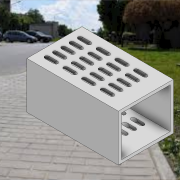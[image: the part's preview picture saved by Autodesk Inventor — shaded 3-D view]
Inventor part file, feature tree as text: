
AUTODESK INVENTOR PART (.ipt)
format: ipt  version: 2021 (Build 250183000, 183)  size: 454,144 bytes
history: native  units: mm
features: sketch x6, extrude x5, plane x2, pattern_linear x1, mirror x1, hole x1, fillet x1, projected_geometry x1
ambient origin geometry x8: Origin, YZ Plane, XZ Plane, XY Plane, X Axis, Y Axis, Z Axis, Center Point
bodies: Solid1 (feature_tree)
feature tree (18):
  sketch  "Sketch1"  dims[d0=45.0mm d1=53.0mm]
  extrude  "Extrusion1"  Depth=53.0mm
  extrude  "Extrusion2"  Depth=85.0mm TaperAngle=0.0deg
  sketch  "Sketch3"  dims[d2=3.0mm d11=85.0mm d12=0.0mm]
  plane  "Work Plane1"
  extrude  "Extrusion3"  Depth=3.0mm
  pattern_linear  "Rectangular Pattern1"  Spacing1=33.0mm  [1 undecoded]
  mirror  "Mirror1"
  plane  "Work Plane2"
  extrude  "Extrusion11"  Depth=50.0mm
  extrude  "Extrusion13"  [1 undecoded]
  hole  "Hole3"  [1 undecoded]
  fillet  "Fillet4"  Radius=3.0mm
  sketch  "Sketch5"  dims[d13=3.0mm d14=0.0mm d16=42.5mm]
  sketch  "Sketch12"  dims[d17=-7.853982mm]
  sketch  "Sketch15"  dims[d19=4.0mm]
  projected_geometry  "Projected Loop7"
  sketch  "Sketch16"  dims[d20=5.0mm d21=33.0mm d22=0.0mm d23=50.0mm d25=8.0mm d26=40.0mm d28=18.0mm d32=-6.5mm d48=3.0mm d49=3.0mm d50=3.0mm d79=3.0mm d80=3.0mm d81=86.0mm d82=0.0mm d83=7.0mm d84=0.0mm d97=15.0mm d98=12.0mm d99=15.0mm d100=0.0mm d101=9.0mm d102=6.0mm d103=15.0mm d104=9.0mm d105=90.0deg d106=8.0mm d107=20.594885mm d108=10.0mm d61=0.5mm d62=0.872665mm d63=0.5mm d64=0.872665mm]
note: 3 required parameter values undecoded (feature->parameter linkage not recoverable at this tier; creation-order binding heuristic only, values carry confidence <= 0.55)
